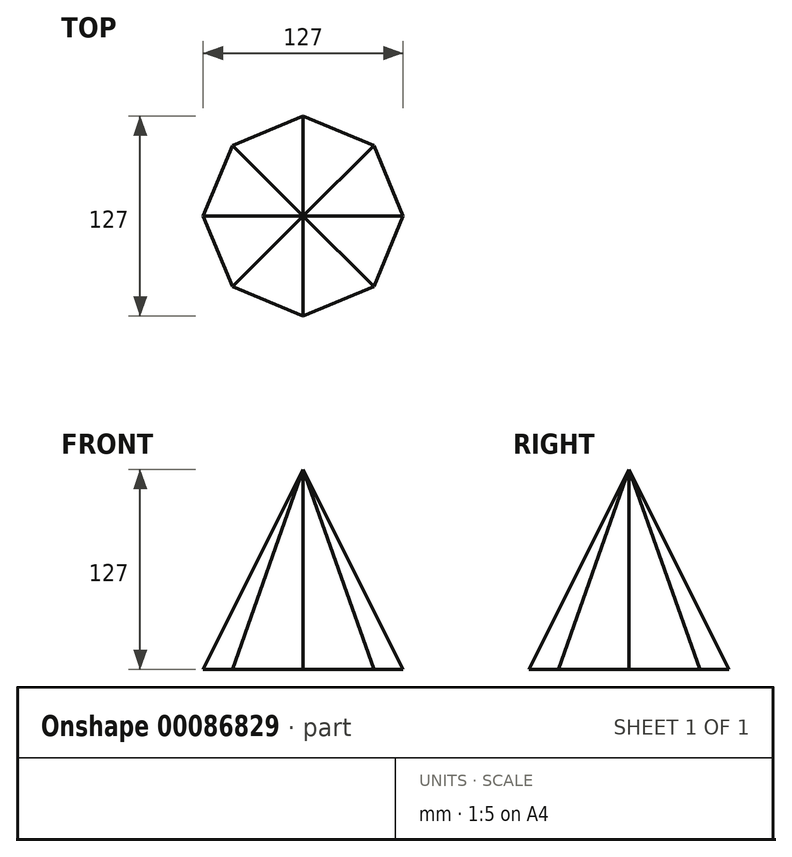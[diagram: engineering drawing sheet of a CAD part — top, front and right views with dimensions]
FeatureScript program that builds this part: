
annotation { "Feature Type Name" : "Feature", "Feature Type Description" : "" }
export const myFeature = defineFeature(function(context is Context, id is Id, definition is map)
    precondition{}
    {
        {
            var Q0;
            Q0=qCreatedBy(makeId("Front.planeOp"),FACE);
            var sketch = newSketch(context, id + "F0", { "sketchPlane" : qUnion([Q0])});
            skPoint(sketch, "E0", {"position": v(0, 127) * mm});
            skSolve(sketch);
        }
        {
            var Q0;
            Q0=qCreatedBy(makeId("Top.planeOp"),FACE);
            var sketch = newSketch(context, id + "F1", { "sketchPlane" : qUnion([Q0])});
            skCircle(sketch, "E1.cCircle", {"center": v(0, 0) * mm, "radius": 63.5 * mm, "construction": true});
            skLineSegment(sketch, "E1.0", {"start": v(0, 63.5) * mm, "end": v(44.9, 44.9) * mm});
            skLineSegment(sketch, "E1.1", {"start": v(44.9, 44.9) * mm, "end": v(63.5, 0) * mm});
            skLineSegment(sketch, "E1.2", {"start": v(63.5, 0) * mm, "end": v(44.9, -44.9) * mm});
            skLineSegment(sketch, "E1.3", {"start": v(44.9, -44.9) * mm, "end": v(0, -63.5) * mm});
            skLineSegment(sketch, "E1.4", {"start": v(0, -63.5) * mm, "end": v(-44.9, -44.9) * mm});
            skLineSegment(sketch, "E1.5", {"start": v(-44.9, -44.9) * mm, "end": v(-63.5, 0) * mm});
            skLineSegment(sketch, "E1.6", {"start": v(-63.5, 0) * mm, "end": v(-44.9, 44.9) * mm});
            skLineSegment(sketch, "E1.7", {"start": v(-44.9, 44.9) * mm, "end": v(0, 63.5) * mm});
            skSolve(sketch);
        }
        {
            var Q0;
            Q0=makeQuery(id+"F1.imprint","IMPRINT",FACE,{"disambiguationData":[TD([[makeQuery(id+"F1.imprint","IMPRINT",EDGE,{"derivedFrom":sQuery(id+"F1.wireOp",EDGE,"E1.0")}),-1.0]])]});
            var Q1;
            Q1=sQuery(id+"F0.wireOp",VERTEX,"E0");
            loft(context, id + "F2", {"sheetProfilesArray" : [{ "sheetProfileEntities" : qUnion([Q0]) }, { "sheetProfileEntities" : qUnion([Q1]) }]});
        }
    });
